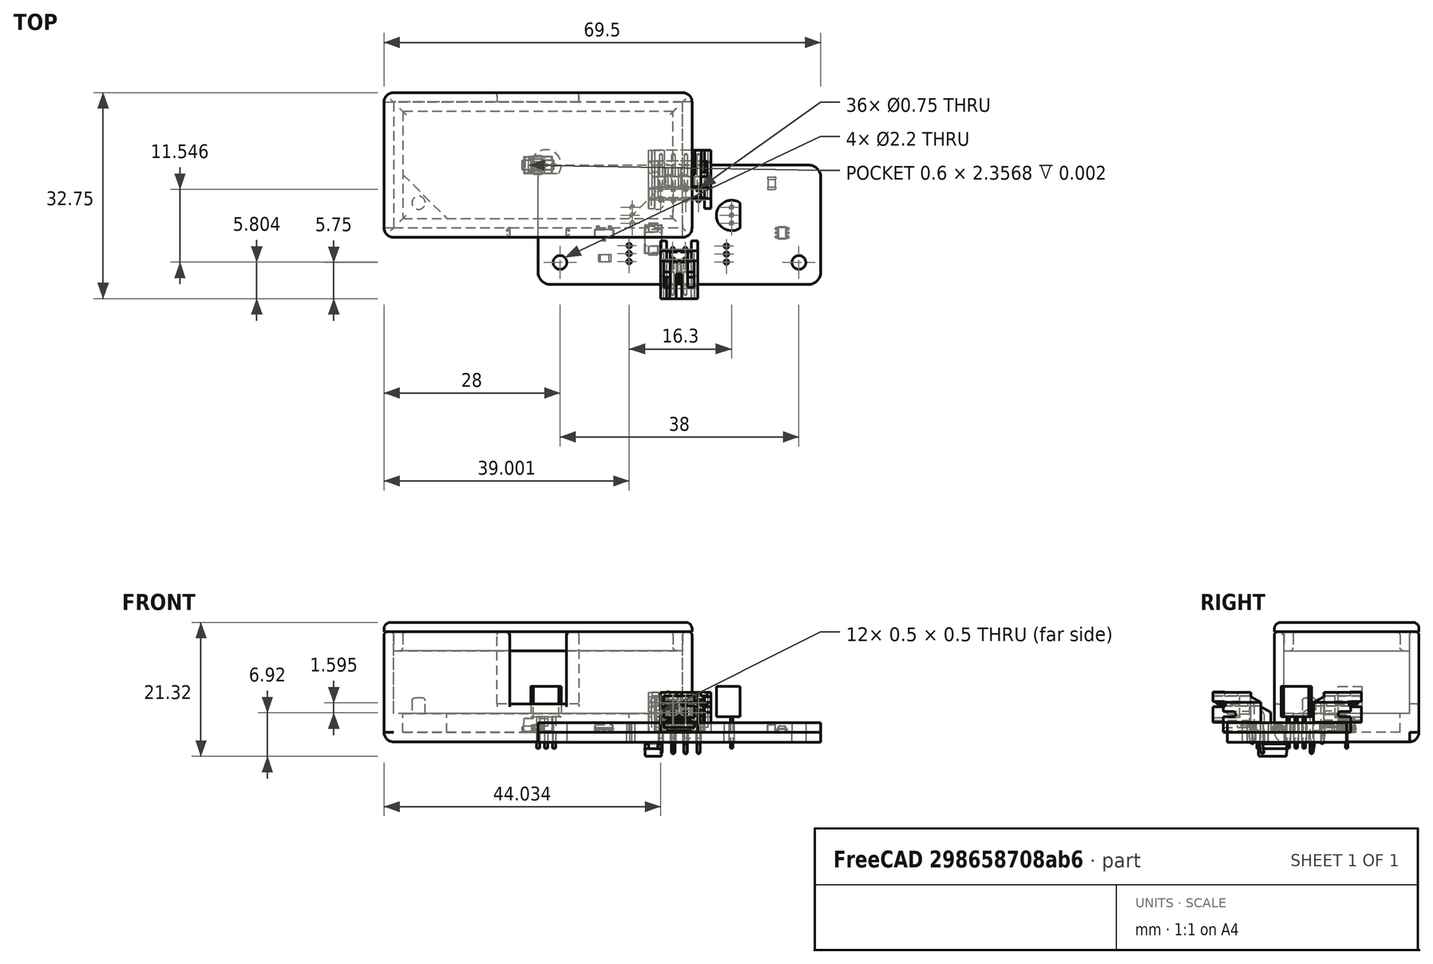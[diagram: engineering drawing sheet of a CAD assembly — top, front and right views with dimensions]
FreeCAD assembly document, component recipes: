
FREECAD ASSEMBLY — COMPONENT RECIPES ("Test2")

This assembly document has 9 components, labeled P0..P8 below (a component is one placed body or linked part). 2 of them carry a construction recipe — the FreeCAD feature program that regenerates the part from scratch, quoted from this document or its linked companion documents; the rest are supplied as boundary geometry only. No exploded tour is included for this assembly.
COMPONENT P0 — geometry summary ("npn-pnp-h-bridge"; no construction recipe available for this part):
  bounding box: 45.0 x 20.3 x 11.1 mm
  tessellated surface: 7,232 triangles
  volume: 8862124490900290044741687870971013986924191587174478991218087669764832598316955017208454054651363328 mm^3 (87241779755121285871774992724642243483395424866212457985545276691758853848768311936437242564706304% of its bounding box)
COMPONENT P1 — recipe-attached ("Body", modeled in this document).
Construction recipe (the document's own serialized feature program — sketch geometry with constraints, then the solid features built on it; lengths are millimeters unless a unit is written):

FEATURE [Sketcher::SketchObject] Sketch
  ArcFitTolerance = 1e-06
  AttachmentSupport = -> [XY_Plane]
  FullyConstrained = true
  MakeInternals = false
  MapMode = 5
  sketch-geometry (4):
    g0: LineSegment StartX=-23 StartY=10 StartZ=0 EndX=-23 EndY=-10 EndZ=0
    g1: LineSegment StartX=-23 StartY=-10 StartZ=0 EndX=23 EndY=-10 EndZ=0
    g2: LineSegment StartX=23 StartY=-10 StartZ=0 EndX=23 EndY=10 EndZ=0
    g3: LineSegment StartX=23 StartY=10 StartZ=0 EndX=-23 EndY=10 EndZ=0
  constraints (11):
    c: Coincident(g0,g1)
    c: Coincident(g1,g2)
    c: Coincident(g2,g3)
    c: Coincident(g3,g0)
    c: Vertical(g0)
    c: Vertical(g2)
    c: Horizontal(g1)
    c: Horizontal(g3)
    c: Distance(g0,g2) = 46
    c: Distance(g1,g3) = 20
    c: Symmetric(g0,g1,g-1)
FEATURE [PartDesign::Pad] Pad  label="Gehäuse"
  Direction = (0,0,1)
  Length = 16
  Length2 = 10
  Profile = -> Sketch
  ReferenceAxis = -> Sketch [N_Axis]
  Refine = true
  Suppressed = false
  Type = 0
FEATURE [PartDesign::Thickness] Thickness
  Base = -> Pad [Face6]
  BaseFeature = -> Pad
  Intersection = false
  Join = 0
  Mode = 0
  Refine = true
  SupportTransform = false
  Suppressed = false
  Value = 1.5
FEATURE [Sketcher::SketchObject] Sketch001  label="pcb-base"
  ArcFitTolerance = 1e-06
  AttachmentSupport = -> [XY_Plane]
  ExternalGeometry = -> [Thickness]
  FullyConstrained = true
  MakeInternals = false
  MapMode = 5
  sketch-geometry (14):
    g0: LineSegment StartX=-23 StartY=10 StartZ=0 EndX=-23 EndY=-10 EndZ=0
    g1: LineSegment StartX=-23 StartY=-10 StartZ=0 EndX=23 EndY=-10 EndZ=0
    g2: LineSegment StartX=23 StartY=-10 StartZ=0 EndX=23 EndY=10 EndZ=0
    g3: LineSegment StartX=23 StartY=10 StartZ=0 EndX=-23 EndY=10 EndZ=0
    g4: LineSegment StartX=-21.5 StartY=8.5 StartZ=0 EndX=-21.5 EndY=-1.51 EndZ=0
    g5: LineSegment StartX=-14.51 StartY=-8.5 StartZ=0 EndX=14.51 EndY=-8.5 EndZ=0
    g6: LineSegment StartX=21.5 StartY=-1.51 StartZ=0 EndX=21.5 EndY=8.5 EndZ=0
    g7: LineSegment StartX=21.5 StartY=8.5 StartZ=0 EndX=-21.5 EndY=8.5 EndZ=0
    g8: ArcOfCircle [constr] CenterX=-14.51 CenterY=-1.51 CenterZ=0 NormalX=0 NormalY=0 NormalZ=1 AngleXU=0 Radius=6.99 StartAngle=3.14159 EndAngle=4.71239
    g9: GeomPoint [constr] X=-21.5 Y=-8.5 Z=0
    g10: LineSegment StartX=-21.5 StartY=-1.51 StartZ=0 EndX=-14.51 EndY=-8.5 EndZ=0
    g11: ArcOfCircle [constr] CenterX=14.51 CenterY=-1.51 CenterZ=0 NormalX=0 NormalY=0 NormalZ=1 AngleXU=0 Radius=6.99 StartAngle=4.71239 EndAngle=6.28319
    g12: GeomPoint [constr] X=21.5 Y=-8.5 Z=0
    g13: LineSegment StartX=14.51 StartY=-8.5 StartZ=0 EndX=21.5 EndY=-1.51 EndZ=0
  constraints (32):
    c: Coincident(g0,g1)
    c: Coincident(g1,g2)
    c: Coincident(g2,g3)
    c: Coincident(g3,g0)
    c: Vertical(g0)
    c: Vertical(g2)
    c: Horizontal(g1)
    c: Horizontal(g3)
    c: Coincident(g0,g-5)
    c: Coincident(g1,g-6)
    c: Coincident(g6,g7)
    c: Coincident(g7,g4)
    c: Vertical(g4)
    c: Vertical(g6)
    c: Horizontal(g5)
    c: Horizontal(g7)
    c: Distance(g4,g6) = 43
    c: Distance(g9,g7) = 17
    c: Symmetric(g4,g12,g-1)
    c: PointOnObject(g9,g4)
    c: PointOnObject(g9,g5)
    c: Tangent(g4,g8) = -1.5708
    c: Tangent(g5,g8) = -1.5708
    c: Coincident(g10,g4)
    c: Coincident(g10,g5)
    c: PointOnObject(g12,g5)
    c: Tangent(g5,g11) = -1.5708
    c: Tangent(g6,g11) = -1.5708
    c: Coincident(g13,g5)
    c: Coincident(g13,g6)
    c: Symmetric(g8,g11,g-2)
    c: DistanceX(g-1,g11) = 14.51
FEATURE [PartDesign::Pad] Pad001  label="PCB-Base"
  BaseFeature = -> Thickness
  Direction = (0,0,1)
  Length = 3
  Length2 = 10
  Profile = -> Sketch001
  ReferenceAxis = -> Sketch001 [N_Axis]
  Refine = true
  Suppressed = false
  Type = 0
FEATURE [PartDesign::Pad] Pad002
  BaseFeature = -> Pad001
  Direction = (0,0,1)
  Length = 3
  Length2 = 10
  Profile = -> Sketch001
  ReferenceAxis = -> Sketch001 [N_Axis]
  Refine = true
  Suppressed = false
  Type = 0
FEATURE [Sketcher::SketchObject] Sketch002
  ArcFitTolerance = 1e-06
  AttachmentSupport = -> [XY_Plane]
  ExternalGeometry = -> [Pad002]
  FullyConstrained = true
  MakeInternals = false
  MapMode = 5
  sketch-geometry (2):
    g0: Circle CenterX=-19 CenterY=-6 CenterZ=0 NormalX=0 NormalY=0 NormalZ=1 AngleXU=0 Radius=1.05
    g1: Circle CenterX=19 CenterY=-6 CenterZ=0 NormalX=0 NormalY=0 NormalZ=1 AngleXU=0 Radius=1.05
  constraints (6):
    c: Diameter(g0) = 2.1
    c: Diameter(g1) = 2.1
    c: DistanceX(g-3,g0) = 4
    c: DistanceY(g-3,g0) = 4
    c: DistanceY(g-4,g1) = 4
    c: DistanceX(g1,g-6) = 4
FEATURE [PartDesign::Pad] Pad003  label="Nubsis"
  BaseFeature = -> Pad002
  Direction = (0,0,1)
  Length = 5.5
  Length2 = 10
  Profile = -> Sketch002
  ReferenceAxis = -> Sketch002 [N_Axis]
  Refine = true
  Suppressed = false
  Type = 0
FEATURE [Sketcher::SketchObject] Sketch003
  ArcFitTolerance = 1e-06
  AttachmentSupport = -> [Pad003]
  ExternalGeometry = -> [Pad003]
  FullyConstrained = true
  MakeInternals = false
  MapMode = 5
  Placement = pos=(0,-11.5,0) rot=(1,0,0;1.5708rad)
  sketch-geometry (4):
    g0: LineSegment StartX=4.5 StartY=24.55 StartZ=0 EndX=-4.5 EndY=24.55 EndZ=0
    g1: LineSegment StartX=-4.5 StartY=24.55 StartZ=0 EndX=-4.5 EndY=4.55 EndZ=0
    g2: LineSegment StartX=-4.5 StartY=4.55 StartZ=0 EndX=4.5 EndY=4.55 EndZ=0
    g3: LineSegment StartX=4.5 StartY=4.55 StartZ=0 EndX=4.5 EndY=24.55 EndZ=0
  constraints (12):
    c: Coincident(g0,g1)
    c: Coincident(g1,g2)
    c: Coincident(g2,g3)
    c: Coincident(g3,g0)
    c: Horizontal(g0)
    c: Horizontal(g2)
    c: Vertical(g1)
    c: Vertical(g3)
    c: Distance(g1,g3) = 9
    c: Distance(g0,g2) = 20
    c: DistanceY(g1,g-3) = -4.55
    c: DistanceX(g0,g-1) = 4.5
FEATURE [PartDesign::Pocket] Pocket  label="Pocket S2B"
  BaseFeature = -> Pad003
  Direction = (0,1,-2e-16)
  Length = 1.5
  Length2 = 5
  Profile = -> Sketch003
  ReferenceAxis = -> Sketch003 [N_Axis]
  Refine = true
  Suppressed = false
  Type = 0
FEATURE [Sketcher::SketchObject] Sketch004
  ArcFitTolerance = 1e-06
  AttachmentSupport = -> [Pocket]
  ExternalGeometry = -> [Pocket]
  FullyConstrained = false
  MakeInternals = false
  MapMode = 5
  Placement = pos=(0,11.5,0) rot=(0,0.707107,0.707107;3.14159rad)
  sketch-geometry (4):
    g0: LineSegment StartX=-6.5 StartY=24.55 StartZ=0 EndX=-6.5 EndY=4.55 EndZ=0
    g1: LineSegment StartX=-6.5 StartY=4.55 StartZ=0 EndX=6.5 EndY=4.55 EndZ=0
    g2: LineSegment StartX=6.5 StartY=4.55 StartZ=0 EndX=6.5 EndY=24.55 EndZ=0
    g3: LineSegment StartX=6.5 StartY=24.55 StartZ=0 EndX=-6.5 EndY=24.55 EndZ=0
  constraints (11):
    c: Coincident(g0,g1)
    c: Coincident(g1,g2)
    c: Coincident(g2,g3)
    c: Coincident(g3,g0)
    c: Vertical(g0)
    c: Vertical(g2)
    c: Horizontal(g1)
    c: Horizontal(g3)
    c: Distance(g0,g2) = 13
    c: Distance(g1,g3) = 20
    c: DistanceY(g0,g-3) = -4.55
FEATURE [PartDesign::Pocket] Pocket001  label="Pocket S4b"
  BaseFeature = -> Pocket
  Direction = (0,-1,2e-16)
  Length = 1.5
  Length2 = 5
  Profile = -> Sketch004
  ReferenceAxis = -> Sketch004 [N_Axis]
  Refine = true
  Suppressed = false
  Type = 0
FEATURE [PartDesign::Fillet] Fillet006  label="Rundung Base"
  Base = -> Pocket001 [Edge6]
  BaseFeature = -> Pocket001
  Radius = 0.5
  Refine = true
  SupportTransform = false
  Suppressed = false
  UseAllEdges = false
FEATURE [PartDesign::Fillet] Fillet007  label="Rundung Nubsis"
  Base = -> Fillet006 [Face28,Face29]
  BaseFeature = -> Fillet006
  Radius = 0.5
  Refine = true
  SupportTransform = false
  Suppressed = false
  UseAllEdges = false
FEATURE [PartDesign::Fillet] Fillet008  label="Rundung Kanten Löcher Unten"
  Base = -> Fillet007 [Edge74,Edge60]
  BaseFeature = -> Fillet007
  Radius = 0.5
  Refine = true
  SupportTransform = false
  Suppressed = false
  UseAllEdges = false
FEATURE [PartDesign::Fillet] Fillet009  label="Rundung Kanten Löcher"
  Base = -> Fillet008 [Edge65,Edge63]
  BaseFeature = -> Fillet008
  Radius = 0.2
  Refine = true
  SupportTransform = false
  Suppressed = false
  UseAllEdges = false
FEATURE [PartDesign::Fillet] Fillet010  label="Rundung Oberkante"
  Base = -> Fillet009 [Edge6,Edge62,Edge12,Edge16,Edge1,Edge10,Edge8,Edge3,Edge11,Edge9,Edge5,Edge52,Edge34,Edge64,Edge63,Edge61,Edge41]
  BaseFeature = -> Fillet009
  Radius = 0.5
  Refine = true
  SupportTransform = false
  Suppressed = false
  UseAllEdges = false
FEATURE [PartDesign::Body] Body
  AllowCompound = false
  Group = -> [Sketch,Pad,Thickness,Sketch001,Pad001,Pad002,Sketch002,Pad003,Sketch003,Pocket,Sketch004,Pocket001,Fillet006,Fillet007,Fillet008,Fillet009,Fillet010]
  Origin = -> Origin
  Tip = -> Fillet010
COMPONENT P2 — recipe-attached ("Deckel", modeled in this document).
Construction recipe (the document's own serialized feature program — sketch geometry with constraints, then the solid features built on it; lengths are millimeters unless a unit is written):

FEATURE [PartDesign::ShapeBinder] CopyPocket001
  Placement = pos=(0,0,15) rot=(0,0,1;0rad)
  TraceSupport = false
FEATURE [Sketcher::SketchObject] Sketch005
  ArcFitTolerance = 1e-06
  AttachmentSupport = -> [CopyPocket001]
  FullyConstrained = true
  MakeInternals = false
  MapMode = 5
  Placement = pos=(0,0,15) rot=(0,0,1;0rad)
  expr: Constraints[8] = 46 mm - 0.05 mm
  expr: Constraints[9] = 20 mm - 0.05 mm
  sketch-geometry (4):
    g0: LineSegment StartX=-22.975 StartY=9.975 StartZ=0 EndX=-22.975 EndY=-9.975 EndZ=0
    g1: LineSegment StartX=-22.975 StartY=-9.975 StartZ=0 EndX=22.975 EndY=-9.975 EndZ=0
    g2: LineSegment StartX=22.975 StartY=-9.975 StartZ=0 EndX=22.975 EndY=9.975 EndZ=0
    g3: LineSegment StartX=22.975 StartY=9.975 StartZ=0 EndX=-22.975 EndY=9.975 EndZ=0
  constraints (11):
    c: Coincident(g0,g1)
    c: Coincident(g1,g2)
    c: Coincident(g2,g3)
    c: Coincident(g3,g0)
    c: Vertical(g0)
    c: Vertical(g2)
    c: Horizontal(g1)
    c: Horizontal(g3)
    c: Distance(g0,g2) = 45.95
    c: Distance(g1,g3) = 19.95
    c: Symmetric(g0,g1,g-1)
FEATURE [PartDesign::Pad] Pad004  label="Kante Deckelinnenseite"
  Direction = (0,0,1)
  Length = 3
  Length2 = 10
  Placement = pos=(0,0,15) rot=(0,0,1;0rad)
  Profile = -> Sketch005
  ReferenceAxis = -> Sketch005 [N_Axis]
  Refine = true
  Reversed = true
  Suppressed = false
  Type = 0
FEATURE [Sketcher::SketchObject] Sketch006
  ArcFitTolerance = 1e-06
  AttachmentSupport = -> [Pad004]
  FullyConstrained = true
  MakeInternals = false
  MapMode = 5
  Placement = pos=(0,0,15) rot=(0,0,1;0rad)
  sketch-geometry (4):
    g0: LineSegment StartX=-21.5 StartY=8.5 StartZ=0 EndX=-21.5 EndY=-8.5 EndZ=0
    g1: LineSegment StartX=-21.5 StartY=-8.5 StartZ=0 EndX=21.5 EndY=-8.5 EndZ=0
    g2: LineSegment StartX=21.5 StartY=-8.5 StartZ=0 EndX=21.5 EndY=8.5 EndZ=0
    g3: LineSegment StartX=21.5 StartY=8.5 StartZ=0 EndX=-21.5 EndY=8.5 EndZ=0
  constraints (11):
    c: Coincident(g0,g1)
    c: Coincident(g1,g2)
    c: Coincident(g2,g3)
    c: Coincident(g3,g0)
    c: Vertical(g0)
    c: Vertical(g2)
    c: Horizontal(g1)
    c: Horizontal(g3)
    c: DistanceX(g3,g3) = 43
    c: DistanceY(g0,g0) = 17
    c: Symmetric(g0,g1,g-1)
FEATURE [PartDesign::Pocket] Pocket002
  BaseFeature = -> Pad004
  Direction = (0,0,-1)
  Length = 5
  Length2 = 5
  Placement = pos=(0,0,15) rot=(0,0,1;0rad)
  Profile = -> Sketch006
  ReferenceAxis = -> Sketch006 [N_Axis]
  Refine = true
  Suppressed = false
  Type = 0
FEATURE [Sketcher::SketchObject] Sketch007
  ArcFitTolerance = 1e-06
  AttachmentSupport = -> [Pocket002]
  FullyConstrained = true
  MakeInternals = false
  MapMode = 5
  Placement = pos=(0,0,15) rot=(0,0,1;0rad)
  sketch-geometry (4):
    g0: LineSegment StartX=-24.5 StartY=11.5 StartZ=0 EndX=-24.5 EndY=-11.5 EndZ=0
    g1: LineSegment StartX=-24.5 StartY=-11.5 StartZ=0 EndX=24.5 EndY=-11.5 EndZ=0
    g2: LineSegment StartX=24.5 StartY=-11.5 StartZ=0 EndX=24.5 EndY=11.5 EndZ=0
    g3: LineSegment StartX=24.5 StartY=11.5 StartZ=0 EndX=-24.5 EndY=11.5 EndZ=0
  constraints (11):
    c: Coincident(g0,g1)
    c: Coincident(g1,g2)
    c: Coincident(g2,g3)
    c: Coincident(g3,g0)
    c: Vertical(g0)
    c: Vertical(g2)
    c: Horizontal(g1)
    c: Horizontal(g3)
    c: Distance(g0,g2) = 49
    c: Distance(g1,g3) = 23
    c: Symmetric(g0,g1,g-1)
FEATURE [PartDesign::Pad] Pad005
  BaseFeature = -> Pocket002
  Direction = (0,0,1)
  Length = 1.5
  Length2 = 10
  Placement = pos=(0,0,15) rot=(0,0,1;0rad)
  Profile = -> Sketch007
  ReferenceAxis = -> Sketch007 [N_Axis]
  Refine = true
  Suppressed = false
  Type = 0
FEATURE [PartDesign::Fillet] Fillet
  Base = -> Pad005 [Edge22,Edge21,Edge26,Edge24]
  BaseFeature = -> Pad005
  Placement = pos=(0,0,15) rot=(0,0,1;0rad)
  Radius = 1.5
  Refine = true
  SupportTransform = false
  Suppressed = false
  UseAllEdges = false
FEATURE [PartDesign::Fillet] Fillet001
  Base = -> Fillet [Edge27]
  BaseFeature = -> Fillet
  Placement = pos=(0,0,15) rot=(0,0,1;0rad)
  Radius = 1
  Refine = true
  SupportTransform = false
  Suppressed = false
  UseAllEdges = false
FEATURE [PartDesign::Fillet] Fillet012  label="Innenrundung Deckel001"
  Base = -> Fillet001 [Edge56,Edge64,Edge55,Edge62,Edge54,Edge60,Edge57,Edge53,Edge20,Edge19,Edge18,Edge17]
  BaseFeature = -> Fillet001
  Placement = pos=(0,0,15) rot=(0,0,1;0rad)
  Radius = 0.5
  Refine = true
  SupportTransform = false
  Suppressed = false
  UseAllEdges = false
FEATURE [Sketcher::SketchObject] Sketch008
  ArcFitTolerance = 1e-06
  AttachmentSupport = -> [Fillet012]
  FullyConstrained = true
  MakeInternals = false
  MapMode = 5
  Placement = pos=(0,0,15) rot=(1,0,0;3.14159rad)
FEATURE [PartDesign::Body] Body002  label="Deckel"
  AllowCompound = false
  Group = -> [CopyPocket001,Sketch005,Pad004,Sketch006,Pocket002,Sketch007,Pad005,Fillet,Fillet001,Fillet012,Sketch008]
  Origin = -> Origin007
  Placement = pos=(0,0,1) rot=(0,0,1;0rad)
  Tip = -> Fillet012
COMPONENT P3 — geometry summary ("C_0805_2012Metric001"; no construction recipe available for this part):
  bounding box: 40.1 x 4.7 x 4.2 mm
  tessellated surface: 940 triangles
  volume: 14 mm^3 (2% of its bounding box)
COMPONENT P4 — geometry summary ("TO-92_Inline001"; no construction recipe available for this part):
  bounding box: 19.0 x 10.2 x 9.8 mm
  tessellated surface: 240 triangles
  volume: 304 mm^3 (16% of its bounding box)
COMPONENT P5 — geometry summary ("R_0805_2012Metric001"; no construction recipe available for this part):
  bounding box: 40.0 x 13.5 x 0.5 mm
  tessellated surface: 2,072 triangles
  volume: 14 mm^3 (6% of its bounding box)
  symmetry: mirror-symmetric across its z mid-plane
COMPONENT P6 — geometry summary ("SOT-024"; no construction recipe available for this part):
  bounding box: 27.1 x 2.6 x 1.2 mm
  tessellated surface: 624 triangles
  volume: 9 mm^3 (10% of its bounding box)
  symmetry: 2-fold rotationally symmetric about the z axis
COMPONENT P7 — geometry summary ("SOT-363_SC-70-007"; no construction recipe available for this part):
  bounding box: 34.7 x 2.0 x 1.0 mm
  tessellated surface: 1,080 triangles
  volume: 5 mm^3 (7% of its bounding box)
  symmetry: 2-fold rotationally symmetric about the z axis; mirror-symmetric across its x mid-plane, y mid-plane
COMPONENT P8 — geometry summary ("D_SMA001"; no construction recipe available for this part):
  bounding box: 25.9 x 8.1 x 2.2 mm
  tessellated surface: 656 triangles
  volume: 105 mm^3 (23% of its bounding box)
PROVENANCE & LICENSES
A FreeCAD (.FCStd) document from a public repository crawl; recipes are the document's own serialized feature recipes (and, for linked parts, companion documents' recipes).
License: unknown-license-file.
